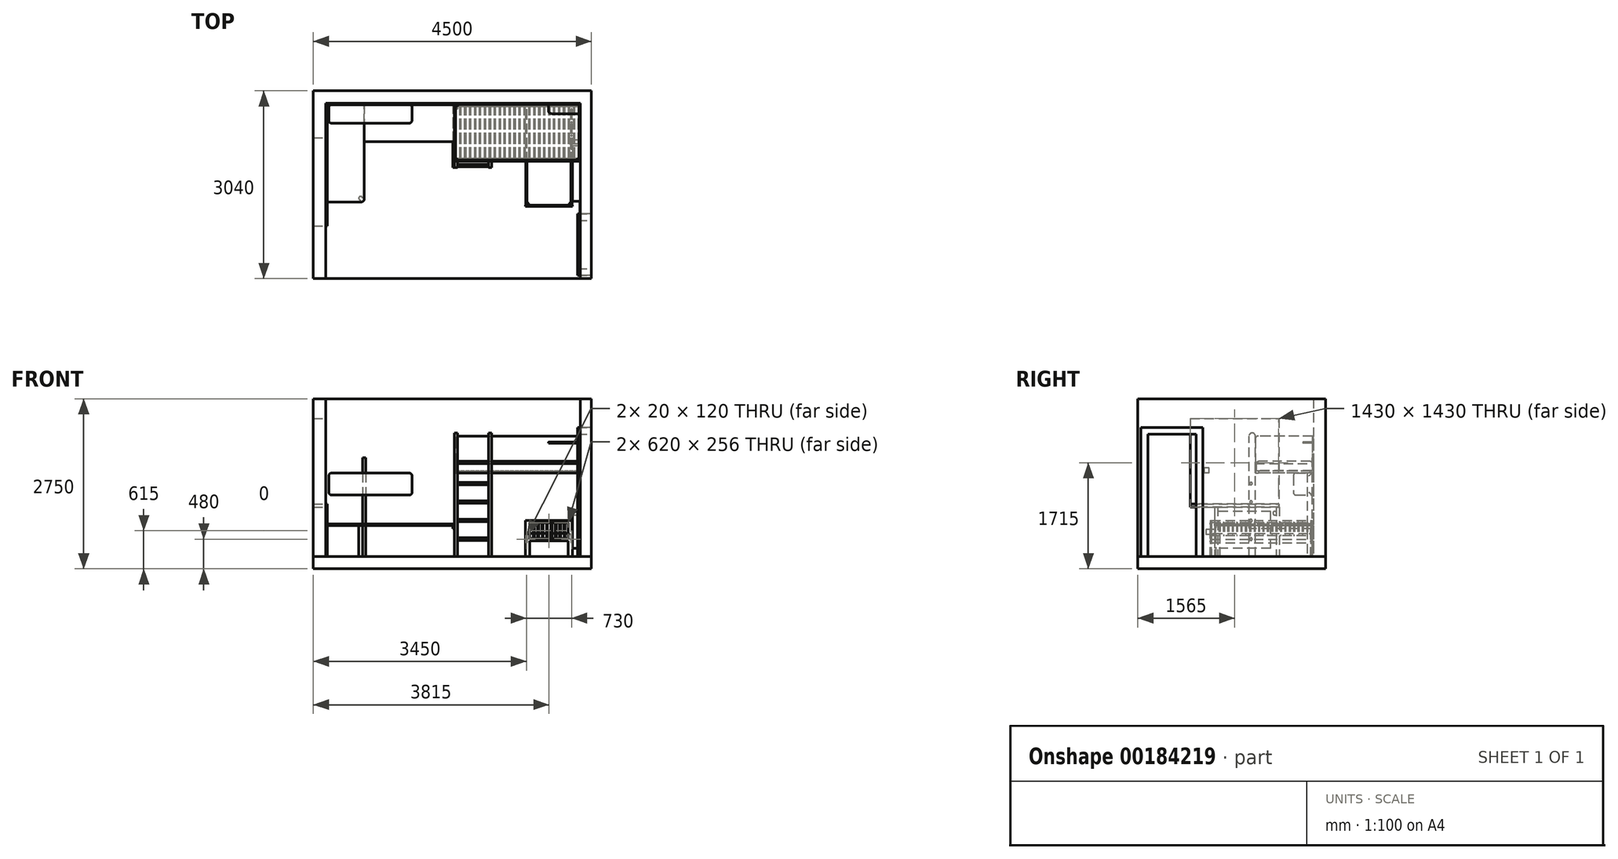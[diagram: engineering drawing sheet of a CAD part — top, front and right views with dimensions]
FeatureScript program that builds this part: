
annotation { "Feature Type Name" : "Feature", "Feature Type Description" : "" }
export const myFeature = defineFeature(function(context is Context, id is Id, definition is map)
    precondition{}
    {
        {
            var Q0;
            Q0=qCreatedBy(makeId("Top.planeOp"),FACE);
            var sketch = newSketch(context, id + "F0", { "sketchPlane" : qUnion([Q0])});
            skLineSegment(sketch, "E0.bottom", {"start": v(-3001.42, -1963.02) * mm, "end": v(-2801.42, -1963.02) * mm});
            skLineSegment(sketch, "E0.left", {"start": v(-3001.42, -1963.02) * mm, "end": v(-3001.42, 1076.98) * mm});
            skLineSegment(sketch, "E0.right", {"start": v(-2801.42, -1963.02) * mm, "end": v(-2801.42, 876.98) * mm});
            skLineSegment(sketch, "E1.bottom", {"start": v(-3001.42, 1076.98) * mm, "end": v(1498.58, 1076.98) * mm});
            skLineSegment(sketch, "E1.top", {"start": v(-2801.42, 876.98) * mm, "end": v(1298.58, 876.98) * mm});
            skLineSegment(sketch, "E2.top", {"start": v(1498.58, -1963.02) * mm, "end": v(1298.58, -1963.02) * mm});
            skLineSegment(sketch, "E2.left", {"start": v(1498.58, 1076.98) * mm, "end": v(1498.58, -1963.02) * mm});
            skLineSegment(sketch, "E2.right", {"start": v(1298.58, 876.98) * mm, "end": v(1298.58, -1963.02) * mm});
            skSolve(sketch);
        }
        {
            var Q0;
            Q0=makeQuery(id+"F0.imprint","IMPRINT",FACE,{"disambiguationData":[TD([[makeQuery(id+"F0.imprint","IMPRINT",EDGE,{"derivedFrom":sQuery(id+"F0.wireOp",EDGE,"E0.bottom")}),1.0]])]});
            extrude(context, id + "F1", {"entities" : qUnion([Q0]), "depth" : 2550 * mm});
        }
        {
            var Q0;
            Q0=makeQuery(id+"F1.opExtrude","SWEPT_FACE",FACE,{"disambiguationData":[OSD([sQuery(id+"F0.wireOp",EDGE,"E2.left")])]});
            var sketch = newSketch(context, id + "F2", { "sketchPlane" : qUnion([Q0])});
            skLineSegment(sketch, "E3.bottom", {"start": v(-1913.02, 0) * mm, "end": v(-913.02, 0) * mm});
            skLineSegment(sketch, "E3.top", {"start": v(-1913.02, 2090) * mm, "end": v(-913.02, 2090) * mm});
            skLineSegment(sketch, "E3.left", {"start": v(-1913.02, 0) * mm, "end": v(-1913.02, 2090) * mm});
            skLineSegment(sketch, "E3.right", {"start": v(-913.02, 0) * mm, "end": v(-913.02, 2090) * mm});
            skSolve(sketch);
        }
        {
            var Q0;
            Q0=makeQuery(id+"F2.imprint","IMPRINT",FACE,{"disambiguationData":[TD([[makeQuery(id+"F2.imprint","IMPRINT",EDGE,{"derivedFrom":sQuery(id+"F2.wireOp",EDGE,"E3.bottom")}),-1.0]])]});
            var Q1;
            Q1=makeQuery(id+"F1.opExtrude","SWEPT_FACE",FACE,{"disambiguationData":[OSD([sQuery(id+"F0.wireOp",EDGE,"E2.right")])]});
            extrude(context, id + "F3", {"entities" : qUnion([Q0, Q1]), "operationType" : NewBodyOperationType.REMOVE, "depth" : 25 * mm, "hasSecondDirection" : true, "secondDirectionBound" : SecondDirectionBoundingType.UP_TO_NEXT, "secondDirectionOppositeDirection" : true, "secondDirectionDepth" : 25 * mm});
        }
        {
            var Q0;
            {var subQ0=sQuery(id+"F0.wireOp",EDGE,"E0.right");var subQ1=sQuery(id+"F0.wireOp",EDGE,"E0.left");var subQ2=sQuery(id+"F0.wireOp",EDGE,"E1.bottom");var subQ3=sQuery(id+"F0.wireOp",EDGE,"E0.bottom");var subQ4=sQuery(id+"F0.wireOp",EDGE,"E1.top");var subQ5=sQuery(id+"F0.wireOp",EDGE,"E2.right");var subQ6=sQuery(id+"F0.wireOp",EDGE,"E2.left");Q0=makeQuery(id+"F3.boolean.opBoolean","SPLIT",FACE,{"disambiguationData":[TD([makeQuery(id+"F1.opExtrude","SWEPT_FACE",FACE,{"disambiguationData":[OSD([subQ3])]})])],"derivedFrom":makeQuery(id+"F1.opExtrude","CAP_FACE",FACE,{"disambiguationData":[OSD([subQ3,subQ1,subQ0,subQ2,subQ4,sQuery(id+"F0.wireOp",EDGE,"E2.top"),subQ6,subQ5])],"isStart":true})});}
            var sketch = newSketch(context, id + "F4", { "sketchPlane" : qUnion([Q0])});
            skLineSegment(sketch, "E4.bottom", {"start": v(-3001.42, 1963.02) * mm, "end": v(1498.58, 1963.02) * mm});
            skLineSegment(sketch, "E4.top", {"start": v(-3001.42, -1076.98) * mm, "end": v(1498.58, -1076.98) * mm});
            skLineSegment(sketch, "E4.left", {"start": v(-3001.42, 1963.02) * mm, "end": v(-3001.42, -1076.98) * mm});
            skLineSegment(sketch, "E4.right", {"start": v(1498.58, 1963.02) * mm, "end": v(1498.58, -1076.98) * mm});
            skSolve(sketch);
        }
        {
            var Q0;
            Q0 = qSketchRegion(id + "F4", true);
            extrude(context, id + "F5", {"entities" : qUnion([Q0]), "depth" : 200 * mm});
        }
        {
            var Q0;
            Q0=makeQuery(id+"F1.opExtrude","SWEPT_FACE",FACE,{"disambiguationData":[OSD([sQuery(id+"F0.wireOp",EDGE,"E0.right")])]});
            var sketch = newSketch(context, id + "F6", { "sketchPlane" : qUnion([Q0])});
            skLineSegment(sketch, "E5.bottom", {"start": v(6034.41, -2246.1) * mm, "end": v(2051.9, -2246.1) * mm});
            skLineSegment(sketch, "E5.top", {"start": v(6034.41, 0) * mm, "end": v(2051.9, 0) * mm});
            skLineSegment(sketch, "E5.left", {"start": v(6034.41, -2246.1) * mm, "end": v(6034.41, 0) * mm});
            skLineSegment(sketch, "E5.right", {"start": v(2051.9, -2246.1) * mm, "end": v(2051.9, 0) * mm});
            skLineSegment(sketch, "E6.bottom", {"start": v(-1113.02, 2230) * mm, "end": v(316.98, 2230) * mm});
            skLineSegment(sketch, "E6.top", {"start": v(-1113.02, 800) * mm, "end": v(316.98, 800) * mm});
            skLineSegment(sketch, "E6.left", {"start": v(-1113.02, 2230) * mm, "end": v(-1113.02, 800) * mm});
            skLineSegment(sketch, "E6.right", {"start": v(316.98, 2230) * mm, "end": v(316.98, 800) * mm});
            skSolve(sketch);
        }
        {
            var Q0;
            Q0 = qSketchRegion(id + "F6", true);
            var Q1;
            Q1=makeQuery(id+"F5.boolean.opBoolean","MERGE",FACE,{"derivedFrom":[makeQuery(id+"F1.opExtrude","SWEPT_FACE",FACE,{"disambiguationData":[OSD([sQuery(id+"F0.wireOp",EDGE,"E0.left")])]}),makeQuery(id+"F5.opExtrude","SWEPT_FACE",FACE,{"disambiguationData":[OSD([sQuery(id+"F4.wireOp",EDGE,"E4.left")])]})]});
            extrude(context, id + "F7", {"entities" : qUnion([Q0]), "operationType" : NewBodyOperationType.REMOVE, "endBound" : BoundingType.UP_TO_SURFACE, "oppositeDirection" : true, "endBoundEntityFace" : qUnion([Q1]), "depth" : 25 * mm});
        }
        {
            var Q0;
            Q0=makeQuery(id+"F5.boolean.opBoolean","MERGE",FACE,{"derivedFrom":[makeQuery(id+"F1.opExtrude","SWEPT_FACE",FACE,{"disambiguationData":[OSD([sQuery(id+"F0.wireOp",EDGE,"E2.left")])]}),makeQuery(id+"F5.opExtrude","SWEPT_FACE",FACE,{"disambiguationData":[OSD([sQuery(id+"F4.wireOp",EDGE,"E4.right")])]})]});
            var sketch = newSketch(context, id + "F8", { "sketchPlane" : qUnion([Q0])});
            skLineSegment(sketch, "E7.bottom", {"start": v(-1803.02, 1980) * mm, "end": v(-1023.02, 1980) * mm});
            skLineSegment(sketch, "E7.left", {"start": v(-1803.02, 1980) * mm, "end": v(-1803.02, 0) * mm});
            skLineSegment(sketch, "E7.right", {"start": v(-1023.02, 1980) * mm, "end": v(-1023.02, 0) * mm});
            skLineSegment(sketch, "E8.bottom", {"start": v(-1913.02, 2090) * mm, "end": v(-913.02, 2090) * mm});
            skLineSegment(sketch, "E8.top", {"start": v(-1913.02, 0) * mm, "end": v(-1803.02, 0) * mm});
            skLineSegment(sketch, "E8.left", {"start": v(-1913.02, 2090) * mm, "end": v(-1913.02, 0) * mm});
            skLineSegment(sketch, "E8.right", {"start": v(-913.02, 2090) * mm, "end": v(-913.02, 0) * mm});
            skLineSegment(sketch, "E9.trimOffspring", {"start": v(-1023.02, 0) * mm, "end": v(-913.02, 0) * mm});
            skSolve(sketch);
        }
        {
            var Q0;
            Q0 = qSketchRegion(id + "F8", true);
            extrude(context, id + "F9", {"entities" : qUnion([Q0]), "oppositeDirection" : true, "depth" : 220 * mm});
        }
        {
            var Q0;
            Q0=makeQuery(id+"F7.boolean.opBoolean","COPY",FACE,{"derivedFrom":makeQuery(id+"F7.opExtrude","SWEPT_FACE",FACE,{"disambiguationData":[OSD([sQuery(id+"F6.wireOp",EDGE,"E6.top")])]})});
            var sketch = newSketch(context, id + "F10", { "sketchPlane" : qUnion([Q0])});
            skLineSegment(sketch, "E10.bottom", {"start": v(-3001.42, 316.98) * mm, "end": v(-2776.42, 316.98) * mm});
            skLineSegment(sketch, "E10.top", {"start": v(-3001.42, -1113.02) * mm, "end": v(-2776.42, -1113.02) * mm});
            skLineSegment(sketch, "E10.left", {"start": v(-3001.42, 316.98) * mm, "end": v(-3001.42, -1113.02) * mm});
            skLineSegment(sketch, "E10.right", {"start": v(-2776.42, 316.98) * mm, "end": v(-2776.42, -1113.02) * mm});
            skSolve(sketch);
        }
        {
            var Q0;
            Q0 = qSketchRegion(id + "F10", true);
            extrude(context, id + "F11", {"entities" : qUnion([Q0]), "depth" : 50 * mm});
        }
        {
            var Q0;
            Q0=makeQuery(id+"F3.boolean.opBoolean","COPY",FACE,{"derivedFrom":makeQuery(id+"F3.opExtrude","CAP_FACE",FACE,{"disambiguationData":[OSD([sQuery(id+"F0.wireOp",EDGE,"E2.right")])],"isStart":false})});
            var sketch = newSketch(context, id + "F12", { "sketchPlane" : qUnion([Q0])});
            skLineSegment(sketch, "E11.bottom", {"start": v(-186.98, 130) * mm, "end": v(713.02, 130) * mm});
            skLineSegment(sketch, "E11.top", {"start": v(-186.98, 730) * mm, "end": v(713.02, 730) * mm});
            skLineSegment(sketch, "E11.left", {"start": v(-186.98, 130) * mm, "end": v(-186.98, 730) * mm});
            skLineSegment(sketch, "E11.right", {"start": v(713.02, 130) * mm, "end": v(713.02, 730) * mm});
            skSolve(sketch);
        }
        {
            var Q0;
            Q0 = qSketchRegion(id + "F12", true);
            extrude(context, id + "F13", {"entities" : qUnion([Q0]), "depth" : 130 * mm});
        }
        {
            var Q0;
            Q0=makeQuery(id+"F3.boolean.opBoolean","COPY",FACE,{"derivedFrom":makeQuery(id+"F3.opExtrude","CAP_FACE",FACE,{"disambiguationData":[OSD([sQuery(id+"F0.wireOp",EDGE,"E2.right")])],"isStart":false})});
            var sketch = newSketch(context, id + "F14", { "sketchPlane" : qUnion([Q0])});
            skCircle(sketch, "E12", {"center": v(-251.98, 700) * mm, "radius": 30 * mm});
            skSolve(sketch);
        }
        {
            var Q0;
            Q0 = qSketchRegion(id + "F14", true);
            extrude(context, id + "F15", {"entities" : qUnion([Q0]), "depth" : 180 * mm});
        }
        {
            var Q0;
            Q0=makeQuery(id+"F3.boolean.opBoolean","COPY",FACE,{"derivedFrom":makeQuery(id+"F3.opExtrude","CAP_FACE",FACE,{"disambiguationData":[OSD([sQuery(id+"F0.wireOp",EDGE,"E2.right")])],"isStart":false})});
            var sketch = newSketch(context, id + "F16", { "sketchPlane" : qUnion([Q0])});
            skLineSegment(sketch, "E13.bottom", {"start": v(713.02, 435) * mm, "end": v(863.02, 435) * mm});
            skLineSegment(sketch, "E13.top", {"start": v(713.02, 355) * mm, "end": v(863.02, 355) * mm});
            skLineSegment(sketch, "E13.left", {"start": v(713.02, 435) * mm, "end": v(713.02, 355) * mm});
            skLineSegment(sketch, "E13.right", {"start": v(863.02, 435) * mm, "end": v(863.02, 355) * mm});
            skSolve(sketch);
        }
        {
            var Q0;
            Q0 = qSketchRegion(id + "F16", true);
            extrude(context, id + "F17", {"entities" : qUnion([Q0]), "depth" : 10 * mm});
        }
        {
            var Q0;
            Q0=makeQuery(id+"F3.boolean.opBoolean","COPY",FACE,{"derivedFrom":makeQuery(id+"F3.opExtrude","CAP_FACE",FACE,{"disambiguationData":[OSD([sQuery(id+"F0.wireOp",EDGE,"E2.right")])],"isStart":false})});
            var sketch = newSketch(context, id + "F18", { "sketchPlane" : qUnion([Q0])});
            skLineSegment(sketch, "E14.bottom", {"start": v(808.02, 1350) * mm, "end": v(888.02, 1350) * mm});
            skLineSegment(sketch, "E14.top", {"start": v(808.02, 1430) * mm, "end": v(888.02, 1430) * mm});
            skLineSegment(sketch, "E14.left", {"start": v(808.02, 1350) * mm, "end": v(808.02, 1430) * mm});
            skLineSegment(sketch, "E14.right", {"start": v(888.02, 1350) * mm, "end": v(888.02, 1430) * mm});
            skSolve(sketch);
        }
        {
            var Q0;
            Q0 = qSketchRegion(id + "F18", true);
            extrude(context, id + "F19", {"entities" : qUnion([Q0]), "depth" : 10 * mm});
        }
        {
            var Q0;
            {var subQ0=sQuery(id+"F0.wireOp",EDGE,"E1.top");Q0=makeQuery(id+"F3.boolean.opBoolean","MERGE",FACE,{"derivedFrom":[makeQuery(id+"F1.opExtrude","SWEPT_FACE",FACE,{"disambiguationData":[OSD([subQ0])]})],"fromTools":[makeQuery(id+"F3.opExtrude","SWEPT_FACE",FACE,{"disambiguationData":[OSD([subQ0,sQuery(id+"F0.wireOp",EDGE,"E2.right")])]})]});}
            var sketch = newSketch(context, id + "F20", { "sketchPlane" : qUnion([Q0])});
            skLineSegment(sketch, "E15.bottom", {"start": v(433.58, 580) * mm, "end": v(1193.58, 580) * mm});
            skLineSegment(sketch, "E15.top", {"start": v(433.58, 0) * mm, "end": v(503.58, 0) * mm});
            skLineSegment(sketch, "E15.left", {"start": v(433.58, 580) * mm, "end": v(433.58, 0) * mm});
            skLineSegment(sketch, "E15.right", {"start": v(1193.58, 580) * mm, "end": v(1193.58, 0) * mm});
            skLineSegment(sketch, "E16.top", {"start": v(503.58, 250) * mm, "end": v(1123.58, 250) * mm});
            skLineSegment(sketch, "E16.left", {"start": v(503.58, 0) * mm, "end": v(503.58, 250) * mm});
            skLineSegment(sketch, "E16.right", {"start": v(1123.58, 0) * mm, "end": v(1123.58, 250) * mm});
            skLineSegment(sketch, "E17.trimOffspring", {"start": v(1123.58, 0) * mm, "end": v(1193.58, 0) * mm});
            skLineSegment(sketch, "E18.bottom", {"start": v(503.58, 287) * mm, "end": v(1123.58, 287) * mm});
            skLineSegment(sketch, "E18.top", {"start": v(503.58, 543) * mm, "end": v(1123.58, 543) * mm});
            skLineSegment(sketch, "E18.left", {"start": v(503.58, 287) * mm, "end": v(503.58, 543) * mm});
            skLineSegment(sketch, "E18.right", {"start": v(1123.58, 287) * mm, "end": v(1123.58, 543) * mm});
            skSolve(sketch);
        }
        {
            var Q0;
            Q0=makeQuery(id+"F20.imprint","IMPRINT",FACE,{"disambiguationData":[TD([[makeQuery(id+"F20.imprint","IMPRINT",EDGE,{"derivedFrom":sQuery(id+"F20.wireOp",EDGE,"E15.bottom")}),-1.0]])]});
            extrude(context, id + "F21", {"entities" : qUnion([Q0]), "depth" : 40 * mm, "hasSecondDirection" : true, "secondDirectionOppositeDirection" : false, "secondDirectionDepth" : 20 * mm});
        }
        {
            var Q0;
            Q0=makeQuery(id+"F21.opExtrude","SWEPT_FACE",FACE,{"disambiguationData":[OSD([sQuery(id+"F20.wireOp",EDGE,"E18.bottom")])]});
            var sketch = newSketch(context, id + "F22", { "sketchPlane" : qUnion([Q0])});
            skCircle(sketch, "E19", {"center": v(566.58, 846.98) * mm, "radius": 8 * mm});
            skCircle(sketch, "E20.1.0.0", {"center": v(637.58, 846.98) * mm, "radius": 8 * mm});
            skCircle(sketch, "E20.2.0.0", {"center": v(708.58, 846.98) * mm, "radius": 8 * mm});
            skCircle(sketch, "E20.3.0.0", {"center": v(779.58, 846.98) * mm, "radius": 8 * mm});
            skCircle(sketch, "E20.4.0.0", {"center": v(850.58, 846.98) * mm, "radius": 8 * mm});
            skCircle(sketch, "E20.5.0.0", {"center": v(921.58, 846.98) * mm, "radius": 8 * mm});
            skCircle(sketch, "E20.6.0.0", {"center": v(992.58, 846.98) * mm, "radius": 8 * mm});
            skCircle(sketch, "E20.7.0.0", {"center": v(1063.58, 846.98) * mm, "radius": 8 * mm});
            skLineSegment(sketch, "E20.direction1", {"start": v(566.58, 846.98) * mm, "end": v(637.58, 846.98) * mm, "construction": true});
            skSolve(sketch);
        }
        {
            var Q0;
            Q0 = qSketchRegion(id + "F22", true);
            var Q1;
            Q1=makeQuery(id+"F21.opExtrude","SWEPT_FACE",FACE,{"disambiguationData":[OSD([sQuery(id+"F20.wireOp",EDGE,"E18.top")])]});
            extrude(context, id + "F23", {"entities" : qUnion([Q0]), "operationType" : NewBodyOperationType.ADD, "endBound" : BoundingType.UP_TO_SURFACE, "endBoundEntityFace" : qUnion([Q1]), "depth" : 25 * mm});
        }
        {
            var Q0;
            Q0 = qSketchRegion(id + "F20", true);
            extrude(context, id + "F24", {"entities" : qUnion([Q0]), "depth" : 1670 * mm, "hasSecondDirection" : true, "secondDirectionOppositeDirection" : false, "secondDirectionDepth" : 1650 * mm});
        }
        {
            var Q0;
            Q0=makeQuery(id+"F24.opExtrude","SWEPT_FACE",FACE,{"disambiguationData":[OSD([sQuery(id+"F20.wireOp",EDGE,"E18.bottom")])]});
            var sketch = newSketch(context, id + "F25", { "sketchPlane" : qUnion([Q0])});
            skCircle(sketch, "E21", {"center": v(568.58, -783.02) * mm, "radius": 8 * mm});
            skCircle(sketch, "E22.1.0.0", {"center": v(639.58, -783.02) * mm, "radius": 8 * mm});
            skCircle(sketch, "E22.2.0.0", {"center": v(710.58, -783.02) * mm, "radius": 8 * mm});
            skCircle(sketch, "E22.3.0.0", {"center": v(781.58, -783.02) * mm, "radius": 8 * mm});
            skCircle(sketch, "E22.4.0.0", {"center": v(852.58, -783.02) * mm, "radius": 8 * mm});
            skCircle(sketch, "E22.5.0.0", {"center": v(923.58, -783.02) * mm, "radius": 8 * mm});
            skCircle(sketch, "E22.6.0.0", {"center": v(994.58, -783.02) * mm, "radius": 8 * mm});
            skCircle(sketch, "E22.7.0.0", {"center": v(1065.58, -783.02) * mm, "radius": 8 * mm});
            skLineSegment(sketch, "E22.direction1", {"start": v(568.58, -783.02) * mm, "end": v(639.58, -783.02) * mm, "construction": true});
            skSolve(sketch);
        }
        {
            var Q0;
            Q0 = qSketchRegion(id + "F25", true);
            var Q1;
            Q1=makeQuery(id+"F24.opExtrude","SWEPT_FACE",FACE,{"disambiguationData":[OSD([sQuery(id+"F20.wireOp",EDGE,"E18.top")])]});
            extrude(context, id + "F26", {"entities" : qUnion([Q0]), "operationType" : NewBodyOperationType.ADD, "endBound" : BoundingType.UP_TO_SURFACE, "endBoundEntityFace" : qUnion([Q1]), "depth" : 25 * mm});
        }
        {
            var Q0;
            Q0=makeQuery(id+"F21.opExtrude","CAP_FACE",FACE,{"disambiguationData":[OSD([sQuery(id+"F20.wireOp",EDGE,"E15.bottom"),sQuery(id+"F20.wireOp",EDGE,"E15.top"),sQuery(id+"F20.wireOp",EDGE,"E15.left"),sQuery(id+"F20.wireOp",EDGE,"E15.right"),sQuery(id+"F20.wireOp",EDGE,"E16.top"),sQuery(id+"F20.wireOp",EDGE,"E16.left"),sQuery(id+"F20.wireOp",EDGE,"E16.right"),sQuery(id+"F20.wireOp",EDGE,"E17.trimOffspring"),sQuery(id+"F20.wireOp",EDGE,"E18.bottom"),sQuery(id+"F20.wireOp",EDGE,"E18.top"),sQuery(id+"F20.wireOp",EDGE,"E18.left"),sQuery(id+"F20.wireOp",EDGE,"E18.right")])],"isStart":false});
            var sketch = newSketch(context, id + "F27", { "sketchPlane" : qUnion([Q0])});
            skLineSegment(sketch, "E23.bottom", {"start": v(438.58, 340) * mm, "end": v(458.58, 340) * mm});
            skLineSegment(sketch, "E23.top", {"start": v(438.58, 220) * mm, "end": v(458.58, 220) * mm});
            skLineSegment(sketch, "E23.left", {"start": v(438.58, 340) * mm, "end": v(438.58, 220) * mm});
            skLineSegment(sketch, "E23.right", {"start": v(458.58, 340) * mm, "end": v(458.58, 220) * mm});
            skLineSegment(sketch, "E24", {"start": v(813.58, 580) * mm, "end": v(813.58, 240.29) * mm, "construction": true});
            skLineSegment(sketch, "E25.MirrorCS", {"start": v(1188.58, 340) * mm, "end": v(1168.58, 340) * mm});
            skLineSegment(sketch, "E26.MirrorCS", {"start": v(1188.58, 220) * mm, "end": v(1168.58, 220) * mm});
            skLineSegment(sketch, "E27.MirrorCS", {"start": v(1168.58, 340) * mm, "end": v(1168.58, 220) * mm});
            skLineSegment(sketch, "E28.MirrorCS", {"start": v(1188.58, 340) * mm, "end": v(1188.58, 220) * mm});
            skLineSegment(sketch, "E29.bottom", {"start": v(1168.58, 580) * mm, "end": v(1188.58, 580) * mm});
            skLineSegment(sketch, "E29.top", {"start": v(1168.58, 550) * mm, "end": v(1188.58, 550) * mm});
            skLineSegment(sketch, "E29.left", {"start": v(1168.58, 580) * mm, "end": v(1168.58, 550) * mm});
            skLineSegment(sketch, "E29.right", {"start": v(1188.58, 580) * mm, "end": v(1188.58, 550) * mm});
            skSolve(sketch);
        }
        {
            var Q0;
            Q0 = qSketchRegion(id + "F27", true);
            extrude(context, id + "F28", {"entities" : qUnion([Q0]), "operationType" : NewBodyOperationType.ADD, "endBound" : BoundingType.UP_TO_NEXT, "depth" : 25 * mm});
        }
        {
            var Q0;
            Q0=makeQuery(id+"F28.opExtrude","SWEPT_FACE",FACE,{"disambiguationData":[OSD([sQuery(id+"F27.wireOp",EDGE,"E25.MirrorCS")])]});
            var sketch = newSketch(context, id + "F29", { "sketchPlane" : qUnion([Q0])});
            skCircle(sketch, "E30", {"center": v(1178.58, 776.98) * mm, "radius": 8 * mm});
            skCircle(sketch, "E31.0.1.0", {"center": v(1178.58, 705.98) * mm, "radius": 8 * mm});
            skCircle(sketch, "E31.0.2.0", {"center": v(1178.58, 634.98) * mm, "radius": 8 * mm});
            skCircle(sketch, "E31.0.3.0", {"center": v(1178.58, 563.98) * mm, "radius": 8 * mm});
            skCircle(sketch, "E31.0.4.0", {"center": v(1178.58, 492.98) * mm, "radius": 8 * mm});
            skCircle(sketch, "E31.0.5.0", {"center": v(1178.58, 421.98) * mm, "radius": 8 * mm});
            skCircle(sketch, "E31.0.6.0", {"center": v(1178.58, 350.98) * mm, "radius": 8 * mm});
            skCircle(sketch, "E31.0.7.0", {"center": v(1178.58, 279.98) * mm, "radius": 8 * mm});
            skCircle(sketch, "E31.0.8.0", {"center": v(1178.58, 208.98) * mm, "radius": 8 * mm});
            skCircle(sketch, "E31.0.9.0", {"center": v(1178.58, 137.98) * mm, "radius": 8 * mm});
            skCircle(sketch, "E31.0.10.0", {"center": v(1178.58, 66.98) * mm, "radius": 8 * mm});
            skCircle(sketch, "E31.0.11.0", {"center": v(1178.58, -4.02) * mm, "radius": 8 * mm});
            skCircle(sketch, "E31.0.12.0", {"center": v(1178.58, -75.02) * mm, "radius": 8 * mm});
            skCircle(sketch, "E31.0.13.0", {"center": v(1178.58, -146.02) * mm, "radius": 8 * mm});
            skCircle(sketch, "E31.0.14.0", {"center": v(1178.58, -217.02) * mm, "radius": 8 * mm});
            skCircle(sketch, "E31.0.15.0", {"center": v(1178.58, -288.02) * mm, "radius": 8 * mm});
            skCircle(sketch, "E31.0.16.0", {"center": v(1178.58, -359.02) * mm, "radius": 8 * mm});
            skCircle(sketch, "E31.0.17.0", {"center": v(1178.58, -430.02) * mm, "radius": 8 * mm});
            skCircle(sketch, "E31.0.18.0", {"center": v(1178.58, -501.02) * mm, "radius": 8 * mm});
            skCircle(sketch, "E31.0.19.0", {"center": v(1178.58, -572.02) * mm, "radius": 8 * mm});
            skCircle(sketch, "E31.0.20.0", {"center": v(1178.58, -643.02) * mm, "radius": 8 * mm});
            skCircle(sketch, "E31.0.21.0", {"center": v(1178.58, -714.02) * mm, "radius": 8 * mm});
            skLineSegment(sketch, "E31.direction1", {"start": v(1178.58, 776.98) * mm, "end": v(1203.58, 776.98) * mm, "construction": true});
            skLineSegment(sketch, "E31.direction2", {"start": v(1178.58, 776.98) * mm, "end": v(1178.58, 705.98) * mm, "construction": true});
            skSolve(sketch);
        }
        {
            var Q0;
            Q0 = qSketchRegion(id + "F29", true);
            extrude(context, id + "F30", {"entities" : qUnion([Q0]), "operationType" : NewBodyOperationType.ADD, "endBound" : BoundingType.UP_TO_NEXT, "depth" : 25 * mm});
        }
        {
            var Q0;
            Q0=makeQuery(id+"F21.opExtrude","CAP_FACE",FACE,{"disambiguationData":[OSD([sQuery(id+"F20.wireOp",EDGE,"E15.bottom"),sQuery(id+"F20.wireOp",EDGE,"E15.top"),sQuery(id+"F20.wireOp",EDGE,"E15.left"),sQuery(id+"F20.wireOp",EDGE,"E15.right"),sQuery(id+"F20.wireOp",EDGE,"E16.top"),sQuery(id+"F20.wireOp",EDGE,"E16.left"),sQuery(id+"F20.wireOp",EDGE,"E16.right"),sQuery(id+"F20.wireOp",EDGE,"E17.trimOffspring"),sQuery(id+"F20.wireOp",EDGE,"E18.bottom"),sQuery(id+"F20.wireOp",EDGE,"E18.top"),sQuery(id+"F20.wireOp",EDGE,"E18.left"),sQuery(id+"F20.wireOp",EDGE,"E18.right")])],"isStart":false});
            var sketch = newSketch(context, id + "F31", { "sketchPlane" : qUnion([Q0])});
            skLineSegment(sketch, "E32.bottom", {"start": v(1168.58, 280) * mm, "end": v(458.58, 280) * mm});
            skLineSegment(sketch, "E32.top", {"start": v(1168.58, 370) * mm, "end": v(458.58, 370) * mm});
            skLineSegment(sketch, "E32.left", {"start": v(1168.58, 280) * mm, "end": v(1168.58, 370) * mm});
            skLineSegment(sketch, "E32.right", {"start": v(458.58, 280) * mm, "end": v(458.58, 370) * mm});
            skSolve(sketch);
        }
        {
            var Q0;
            Q0 = qSketchRegion(id + "F31", true);
            var Q1;
            Q1=makeQuery(id+"F24.opExtrude","CAP_FACE",FACE,{"disambiguationData":[OSD([sQuery(id+"F20.wireOp",EDGE,"E15.bottom"),sQuery(id+"F20.wireOp",EDGE,"E15.top"),sQuery(id+"F20.wireOp",EDGE,"E15.left"),sQuery(id+"F20.wireOp",EDGE,"E15.right"),sQuery(id+"F20.wireOp",EDGE,"E16.top"),sQuery(id+"F20.wireOp",EDGE,"E16.left"),sQuery(id+"F20.wireOp",EDGE,"E16.right"),sQuery(id+"F20.wireOp",EDGE,"E17.trimOffspring"),sQuery(id+"F20.wireOp",EDGE,"E18.bottom"),sQuery(id+"F20.wireOp",EDGE,"E18.top"),sQuery(id+"F20.wireOp",EDGE,"E18.left"),sQuery(id+"F20.wireOp",EDGE,"E18.right")])],"isStart":true});
            extrude(context, id + "F32", {"entities" : qUnion([Q0]), "endBound" : BoundingType.UP_TO_SURFACE, "endBoundEntityFace" : qUnion([Q1]), "depth" : 25 * mm});
        }
        {
            var Q0;
            Q0=makeQuery(id+"F3.boolean.opBoolean","COPY",FACE,{"derivedFrom":makeQuery(id+"F3.opExtrude","CAP_FACE",FACE,{"disambiguationData":[OSD([sQuery(id+"F0.wireOp",EDGE,"E2.right")])],"isStart":false})});
            var sketch = newSketch(context, id + "F33", { "sketchPlane" : qUnion([Q0])});
            skLineSegment(sketch, "E33.bottom", {"start": v(-876.98, 1950) * mm, "end": v(-856.98, 1950) * mm});
            skLineSegment(sketch, "E33.top", {"start": v(-876.98, 1350) * mm, "end": v(-856.98, 1350) * mm});
            skLineSegment(sketch, "E33.left", {"start": v(-876.98, 1950) * mm, "end": v(-876.98, 1350) * mm});
            skLineSegment(sketch, "E33.right", {"start": v(-856.98, 1950) * mm, "end": v(-856.98, 1350) * mm});
            skLineSegment(sketch, "E34.bottom", {"start": v(-856.98, 1350) * mm, "end": v(-826.98, 1350) * mm});
            skLineSegment(sketch, "E34.top", {"start": v(-856.98, 1380) * mm, "end": v(-826.98, 1380) * mm});
            skLineSegment(sketch, "E34.left", {"start": v(-856.98, 1350) * mm, "end": v(-856.98, 1380) * mm});
            skLineSegment(sketch, "E34.right", {"start": v(-826.98, 1350) * mm, "end": v(-826.98, 1380) * mm});
            skLineSegment(sketch, "E35.bottom", {"start": v(-856.98, 1380) * mm, "end": v(43.02, 1380) * mm});
            skLineSegment(sketch, "E35.top", {"start": v(-856.98, 1390) * mm, "end": v(43.02, 1390) * mm});
            skLineSegment(sketch, "E35.left", {"start": v(-856.98, 1380) * mm, "end": v(-856.98, 1390) * mm});
            skLineSegment(sketch, "E35.right", {"start": v(43.02, 1380) * mm, "end": v(43.02, 1390) * mm});
            skLineSegment(sketch, "E36.bottom", {"start": v(43.02, 1380) * mm, "end": v(13.02, 1380) * mm});
            skLineSegment(sketch, "E36.top", {"start": v(43.02, 1350) * mm, "end": v(13.02, 1350) * mm});
            skLineSegment(sketch, "E36.left", {"start": v(43.02, 1380) * mm, "end": v(43.02, 1350) * mm});
            skLineSegment(sketch, "E36.right", {"start": v(13.02, 1380) * mm, "end": v(13.02, 1350) * mm});
            skLineSegment(sketch, "E37.bottom", {"start": v(43.02, 1350) * mm, "end": v(63.02, 1350) * mm});
            skLineSegment(sketch, "E37.top", {"start": v(43.02, 1500) * mm, "end": v(63.02, 1500) * mm});
            skLineSegment(sketch, "E37.left", {"start": v(43.02, 1350) * mm, "end": v(43.02, 1500) * mm});
            skLineSegment(sketch, "E37.right", {"start": v(63.02, 1350) * mm, "end": v(63.02, 1500) * mm});
            skSolve(sketch);
        }
        {
            var Q0;
            Q0 = qSketchRegion(id + "F33", true);
            extrude(context, id + "F34", {"entities" : qUnion([Q0]), "depth" : 2020 * mm, "hasSecondDirection" : true, "secondDirectionOppositeDirection" : false, "secondDirectionDepth" : 20 * mm});
        }
        {
            var Q0;
            Q0=makeQuery(id+"F3.boolean.opBoolean","COPY",FACE,{"derivedFrom":makeQuery(id+"F3.opExtrude","CAP_FACE",FACE,{"disambiguationData":[OSD([sQuery(id+"F0.wireOp",EDGE,"E2.right")])],"isStart":false})});
            var sketch = newSketch(context, id + "F35", { "sketchPlane" : qUnion([Q0])});
            skLineSegment(sketch, "E38.bottom", {"start": v(-876.98, 1950) * mm, "end": v(63.02, 1950) * mm});
            skLineSegment(sketch, "E38.top", {"start": v(-876.98, 1350) * mm, "end": v(63.02, 1350) * mm});
            skLineSegment(sketch, "E38.left", {"start": v(-876.98, 1950) * mm, "end": v(-876.98, 1350) * mm});
            skLineSegment(sketch, "E38.right", {"start": v(63.02, 1950) * mm, "end": v(63.02, 1350) * mm});
            skSolve(sketch);
        }
        {
            var Q0;
            Q0 = qSketchRegion(id + "F35", true);
            extrude(context, id + "F36", {"entities" : qUnion([Q0]), "operationType" : NewBodyOperationType.ADD, "depth" : 20 * mm});
        }
        {
            var Q0;
            Q0=makeQuery(id+"F34.opExtrude","SWEPT_FACE",FACE,{"disambiguationData":[OSD([sQuery(id+"F33.wireOp",EDGE,"E35.top")])]});
            var sketch = newSketch(context, id + "F37", { "sketchPlane" : qUnion([Q0])});
            skLineSegment(sketch, "E39.bottom", {"start": v(-636.42, 856.98) * mm, "end": v(-616.42, 856.98) * mm});
            skLineSegment(sketch, "E39.top", {"start": v(-636.42, -43.02) * mm, "end": v(-616.42, -43.02) * mm});
            skLineSegment(sketch, "E39.left", {"start": v(-636.42, 856.98) * mm, "end": v(-636.42, -43.02) * mm});
            skLineSegment(sketch, "E39.right", {"start": v(-616.42, 856.98) * mm, "end": v(-616.42, -43.02) * mm});
            skLineSegment(sketch, "E40.1.0.0", {"start": v(-536.42, 856.98) * mm, "end": v(-536.42, -43.02) * mm});
            skLineSegment(sketch, "E40.1.0.1", {"start": v(-556.42, 856.98) * mm, "end": v(-556.42, -43.02) * mm});
            skLineSegment(sketch, "E40.1.0.2", {"start": v(-556.42, -43.02) * mm, "end": v(-536.42, -43.02) * mm});
            skLineSegment(sketch, "E40.1.0.3", {"start": v(-556.42, 856.98) * mm, "end": v(-536.42, 856.98) * mm});
            skLineSegment(sketch, "E40.2.0.0", {"start": v(-456.42, 856.98) * mm, "end": v(-456.42, -43.02) * mm});
            skLineSegment(sketch, "E40.2.0.1", {"start": v(-476.42, 856.98) * mm, "end": v(-476.42, -43.02) * mm});
            skLineSegment(sketch, "E40.2.0.2", {"start": v(-476.42, -43.02) * mm, "end": v(-456.42, -43.02) * mm});
            skLineSegment(sketch, "E40.2.0.3", {"start": v(-476.42, 856.98) * mm, "end": v(-456.42, 856.98) * mm});
            skLineSegment(sketch, "E40.3.0.0", {"start": v(-376.42, 856.98) * mm, "end": v(-376.42, -43.02) * mm});
            skLineSegment(sketch, "E40.3.0.1", {"start": v(-396.42, 856.98) * mm, "end": v(-396.42, -43.02) * mm});
            skLineSegment(sketch, "E40.3.0.2", {"start": v(-396.42, -43.02) * mm, "end": v(-376.42, -43.02) * mm});
            skLineSegment(sketch, "E40.3.0.3", {"start": v(-396.42, 856.98) * mm, "end": v(-376.42, 856.98) * mm});
            skLineSegment(sketch, "E40.4.0.0", {"start": v(-296.42, 856.98) * mm, "end": v(-296.42, -43.02) * mm});
            skLineSegment(sketch, "E40.4.0.1", {"start": v(-316.42, 856.98) * mm, "end": v(-316.42, -43.02) * mm});
            skLineSegment(sketch, "E40.4.0.2", {"start": v(-316.42, -43.02) * mm, "end": v(-296.42, -43.02) * mm});
            skLineSegment(sketch, "E40.4.0.3", {"start": v(-316.42, 856.98) * mm, "end": v(-296.42, 856.98) * mm});
            skLineSegment(sketch, "E40.5.0.0", {"start": v(-216.42, 856.98) * mm, "end": v(-216.42, -43.02) * mm});
            skLineSegment(sketch, "E40.5.0.1", {"start": v(-236.42, 856.98) * mm, "end": v(-236.42, -43.02) * mm});
            skLineSegment(sketch, "E40.5.0.2", {"start": v(-236.42, -43.02) * mm, "end": v(-216.42, -43.02) * mm});
            skLineSegment(sketch, "E40.5.0.3", {"start": v(-236.42, 856.98) * mm, "end": v(-216.42, 856.98) * mm});
            skLineSegment(sketch, "E40.6.0.0", {"start": v(-136.42, 856.98) * mm, "end": v(-136.42, -43.02) * mm});
            skLineSegment(sketch, "E40.6.0.1", {"start": v(-156.42, 856.98) * mm, "end": v(-156.42, -43.02) * mm});
            skLineSegment(sketch, "E40.6.0.2", {"start": v(-156.42, -43.02) * mm, "end": v(-136.42, -43.02) * mm});
            skLineSegment(sketch, "E40.6.0.3", {"start": v(-156.42, 856.98) * mm, "end": v(-136.42, 856.98) * mm});
            skLineSegment(sketch, "E40.7.0.0", {"start": v(-56.42, 856.98) * mm, "end": v(-56.42, -43.02) * mm});
            skLineSegment(sketch, "E40.7.0.1", {"start": v(-76.42, 856.98) * mm, "end": v(-76.42, -43.02) * mm});
            skLineSegment(sketch, "E40.7.0.2", {"start": v(-76.42, -43.02) * mm, "end": v(-56.42, -43.02) * mm});
            skLineSegment(sketch, "E40.7.0.3", {"start": v(-76.42, 856.98) * mm, "end": v(-56.42, 856.98) * mm});
            skLineSegment(sketch, "E40.8.0.0", {"start": v(23.58, 856.98) * mm, "end": v(23.58, -43.02) * mm});
            skLineSegment(sketch, "E40.8.0.1", {"start": v(3.58, 856.98) * mm, "end": v(3.58, -43.02) * mm});
            skLineSegment(sketch, "E40.8.0.2", {"start": v(3.58, -43.02) * mm, "end": v(23.58, -43.02) * mm});
            skLineSegment(sketch, "E40.8.0.3", {"start": v(3.58, 856.98) * mm, "end": v(23.58, 856.98) * mm});
            skLineSegment(sketch, "E40.9.0.0", {"start": v(103.58, 856.98) * mm, "end": v(103.58, -43.02) * mm});
            skLineSegment(sketch, "E40.9.0.1", {"start": v(83.58, 856.98) * mm, "end": v(83.58, -43.02) * mm});
            skLineSegment(sketch, "E40.9.0.2", {"start": v(83.58, -43.02) * mm, "end": v(103.58, -43.02) * mm});
            skLineSegment(sketch, "E40.9.0.3", {"start": v(83.58, 856.98) * mm, "end": v(103.58, 856.98) * mm});
            skLineSegment(sketch, "E40.10.0.0", {"start": v(183.58, 856.98) * mm, "end": v(183.58, -43.02) * mm});
            skLineSegment(sketch, "E40.10.0.1", {"start": v(163.58, 856.98) * mm, "end": v(163.58, -43.02) * mm});
            skLineSegment(sketch, "E40.10.0.2", {"start": v(163.58, -43.02) * mm, "end": v(183.58, -43.02) * mm});
            skLineSegment(sketch, "E40.10.0.3", {"start": v(163.58, 856.98) * mm, "end": v(183.58, 856.98) * mm});
            skLineSegment(sketch, "E40.11.0.0", {"start": v(263.58, 856.98) * mm, "end": v(263.58, -43.02) * mm});
            skLineSegment(sketch, "E40.11.0.1", {"start": v(243.58, 856.98) * mm, "end": v(243.58, -43.02) * mm});
            skLineSegment(sketch, "E40.11.0.2", {"start": v(243.58, -43.02) * mm, "end": v(263.58, -43.02) * mm});
            skLineSegment(sketch, "E40.11.0.3", {"start": v(243.58, 856.98) * mm, "end": v(263.58, 856.98) * mm});
            skLineSegment(sketch, "E40.12.0.0", {"start": v(343.58, 856.98) * mm, "end": v(343.58, -43.02) * mm});
            skLineSegment(sketch, "E40.12.0.1", {"start": v(323.58, 856.98) * mm, "end": v(323.58, -43.02) * mm});
            skLineSegment(sketch, "E40.12.0.2", {"start": v(323.58, -43.02) * mm, "end": v(343.58, -43.02) * mm});
            skLineSegment(sketch, "E40.12.0.3", {"start": v(323.58, 856.98) * mm, "end": v(343.58, 856.98) * mm});
            skLineSegment(sketch, "E40.13.0.0", {"start": v(423.58, 856.98) * mm, "end": v(423.58, -43.02) * mm});
            skLineSegment(sketch, "E40.13.0.1", {"start": v(403.58, 856.98) * mm, "end": v(403.58, -43.02) * mm});
            skLineSegment(sketch, "E40.13.0.2", {"start": v(403.58, -43.02) * mm, "end": v(423.58, -43.02) * mm});
            skLineSegment(sketch, "E40.13.0.3", {"start": v(403.58, 856.98) * mm, "end": v(423.58, 856.98) * mm});
            skLineSegment(sketch, "E40.14.0.0", {"start": v(503.58, 856.98) * mm, "end": v(503.58, -43.02) * mm});
            skLineSegment(sketch, "E40.14.0.1", {"start": v(483.58, 856.98) * mm, "end": v(483.58, -43.02) * mm});
            skLineSegment(sketch, "E40.14.0.2", {"start": v(483.58, -43.02) * mm, "end": v(503.58, -43.02) * mm});
            skLineSegment(sketch, "E40.14.0.3", {"start": v(483.58, 856.98) * mm, "end": v(503.58, 856.98) * mm});
            skLineSegment(sketch, "E40.15.0.0", {"start": v(583.58, 856.98) * mm, "end": v(583.58, -43.02) * mm});
            skLineSegment(sketch, "E40.15.0.1", {"start": v(563.58, 856.98) * mm, "end": v(563.58, -43.02) * mm});
            skLineSegment(sketch, "E40.15.0.2", {"start": v(563.58, -43.02) * mm, "end": v(583.58, -43.02) * mm});
            skLineSegment(sketch, "E40.15.0.3", {"start": v(563.58, 856.98) * mm, "end": v(583.58, 856.98) * mm});
            skLineSegment(sketch, "E40.16.0.0", {"start": v(663.58, 856.98) * mm, "end": v(663.58, -43.02) * mm});
            skLineSegment(sketch, "E40.16.0.1", {"start": v(643.58, 856.98) * mm, "end": v(643.58, -43.02) * mm});
            skLineSegment(sketch, "E40.16.0.2", {"start": v(643.58, -43.02) * mm, "end": v(663.58, -43.02) * mm});
            skLineSegment(sketch, "E40.16.0.3", {"start": v(643.58, 856.98) * mm, "end": v(663.58, 856.98) * mm});
            skLineSegment(sketch, "E40.17.0.0", {"start": v(743.58, 856.98) * mm, "end": v(743.58, -43.02) * mm});
            skLineSegment(sketch, "E40.17.0.1", {"start": v(723.58, 856.98) * mm, "end": v(723.58, -43.02) * mm});
            skLineSegment(sketch, "E40.17.0.2", {"start": v(723.58, -43.02) * mm, "end": v(743.58, -43.02) * mm});
            skLineSegment(sketch, "E40.17.0.3", {"start": v(723.58, 856.98) * mm, "end": v(743.58, 856.98) * mm});
            skLineSegment(sketch, "E40.18.0.0", {"start": v(823.58, 856.98) * mm, "end": v(823.58, -43.02) * mm});
            skLineSegment(sketch, "E40.18.0.1", {"start": v(803.58, 856.98) * mm, "end": v(803.58, -43.02) * mm});
            skLineSegment(sketch, "E40.18.0.2", {"start": v(803.58, -43.02) * mm, "end": v(823.58, -43.02) * mm});
            skLineSegment(sketch, "E40.18.0.3", {"start": v(803.58, 856.98) * mm, "end": v(823.58, 856.98) * mm});
            skLineSegment(sketch, "E40.19.0.0", {"start": v(903.58, 856.98) * mm, "end": v(903.58, -43.02) * mm});
            skLineSegment(sketch, "E40.19.0.1", {"start": v(883.58, 856.98) * mm, "end": v(883.58, -43.02) * mm});
            skLineSegment(sketch, "E40.19.0.2", {"start": v(883.58, -43.02) * mm, "end": v(903.58, -43.02) * mm});
            skLineSegment(sketch, "E40.19.0.3", {"start": v(883.58, 856.98) * mm, "end": v(903.58, 856.98) * mm});
            skLineSegment(sketch, "E40.20.0.0", {"start": v(983.58, 856.98) * mm, "end": v(983.58, -43.02) * mm});
            skLineSegment(sketch, "E40.20.0.1", {"start": v(963.58, 856.98) * mm, "end": v(963.58, -43.02) * mm});
            skLineSegment(sketch, "E40.20.0.2", {"start": v(963.58, -43.02) * mm, "end": v(983.58, -43.02) * mm});
            skLineSegment(sketch, "E40.20.0.3", {"start": v(963.58, 856.98) * mm, "end": v(983.58, 856.98) * mm});
            skLineSegment(sketch, "E40.21.0.0", {"start": v(1063.58, 856.98) * mm, "end": v(1063.58, -43.02) * mm});
            skLineSegment(sketch, "E40.21.0.1", {"start": v(1043.58, 856.98) * mm, "end": v(1043.58, -43.02) * mm});
            skLineSegment(sketch, "E40.21.0.2", {"start": v(1043.58, -43.02) * mm, "end": v(1063.58, -43.02) * mm});
            skLineSegment(sketch, "E40.21.0.3", {"start": v(1043.58, 856.98) * mm, "end": v(1063.58, 856.98) * mm});
            skLineSegment(sketch, "E40.22.0.0", {"start": v(1143.58, 856.98) * mm, "end": v(1143.58, -43.02) * mm});
            skLineSegment(sketch, "E40.22.0.1", {"start": v(1123.58, 856.98) * mm, "end": v(1123.58, -43.02) * mm});
            skLineSegment(sketch, "E40.22.0.2", {"start": v(1123.58, -43.02) * mm, "end": v(1143.58, -43.02) * mm});
            skLineSegment(sketch, "E40.22.0.3", {"start": v(1123.58, 856.98) * mm, "end": v(1143.58, 856.98) * mm});
            skLineSegment(sketch, "E40.23.0.0", {"start": v(1223.58, 856.98) * mm, "end": v(1223.58, -43.02) * mm});
            skLineSegment(sketch, "E40.23.0.1", {"start": v(1203.58, 856.98) * mm, "end": v(1203.58, -43.02) * mm});
            skLineSegment(sketch, "E40.23.0.2", {"start": v(1203.58, -43.02) * mm, "end": v(1223.58, -43.02) * mm});
            skLineSegment(sketch, "E40.23.0.3", {"start": v(1203.58, 856.98) * mm, "end": v(1223.58, 856.98) * mm});
            skLineSegment(sketch, "E40.24.0.0", {"start": v(1303.58, 856.98) * mm, "end": v(1303.58, -43.02) * mm});
            skLineSegment(sketch, "E40.24.0.1", {"start": v(1283.58, 856.98) * mm, "end": v(1283.58, -43.02) * mm});
            skLineSegment(sketch, "E40.24.0.2", {"start": v(1283.58, -43.02) * mm, "end": v(1303.58, -43.02) * mm});
            skLineSegment(sketch, "E40.24.0.3", {"start": v(1283.58, 856.98) * mm, "end": v(1303.58, 856.98) * mm});
            skLineSegment(sketch, "E40.direction1", {"start": v(-636.42, -43.02) * mm, "end": v(-556.42, -43.02) * mm, "construction": true});
            skSolve(sketch);
        }
        {
            var Q0;
            Q0 = qSketchRegion(id + "F37", true);
            extrude(context, id + "F38", {"entities" : qUnion([Q0]), "operationType" : NewBodyOperationType.REMOVE, "oppositeDirection" : true, "depth" : 10 * mm});
        }
        {
            var Q0;
            Q0=makeQuery(id+"F3.boolean.opBoolean","COPY",FACE,{"derivedFrom":makeQuery(id+"F3.opExtrude","CAP_FACE",FACE,{"disambiguationData":[OSD([sQuery(id+"F0.wireOp",EDGE,"E2.right")])],"isStart":false})});
            var sketch = newSketch(context, id + "F39", { "sketchPlane" : qUnion([Q0])});
            skLineSegment(sketch, "E41.bottom", {"start": v(63.02, 1500) * mm, "end": v(-876.98, 1500) * mm});
            skLineSegment(sketch, "E41.top", {"start": v(63.02, 1350) * mm, "end": v(-876.98, 1350) * mm});
            skLineSegment(sketch, "E41.left", {"start": v(63.02, 1500) * mm, "end": v(63.02, 1350) * mm});
            skLineSegment(sketch, "E41.right", {"start": v(-876.98, 1500) * mm, "end": v(-876.98, 1350) * mm});
            skSolve(sketch);
        }
        {
            var Q0;
            Q0 = qSketchRegion(id + "F39", true);
            extrude(context, id + "F40", {"entities" : qUnion([Q0]), "depth" : 2040 * mm, "hasSecondDirection" : true, "secondDirectionOppositeDirection" : false, "secondDirectionDepth" : 2020 * mm});
        }
        {
            var Q0;
            Q0=makeQuery(id+"F34.opExtrude","SWEPT_FACE",FACE,{"disambiguationData":[OSD([sQuery(id+"F33.wireOp",EDGE,"E37.top")])]});
            var sketch = newSketch(context, id + "F41", { "sketchPlane" : qUnion([Q0])});
            skLineSegment(sketch, "E42.bottom", {"start": v(-715.78, -63.02) * mm, "end": v(-665.78, -63.02) * mm});
            skLineSegment(sketch, "E42.top", {"start": v(-715.78, -163.02) * mm, "end": v(-665.78, -163.02) * mm});
            skLineSegment(sketch, "E42.left", {"start": v(-715.78, -63.02) * mm, "end": v(-715.78, -163.02) * mm});
            skLineSegment(sketch, "E42.right", {"start": v(-665.78, -63.02) * mm, "end": v(-665.78, -163.02) * mm});
            skLineSegment(sketch, "E43.bottom", {"start": v(-165.78, -63.02) * mm, "end": v(-115.78, -63.02) * mm});
            skLineSegment(sketch, "E43.top", {"start": v(-165.78, -163.02) * mm, "end": v(-115.78, -163.02) * mm});
            skLineSegment(sketch, "E43.left", {"start": v(-165.78, -63.02) * mm, "end": v(-165.78, -163.02) * mm});
            skLineSegment(sketch, "E43.right", {"start": v(-115.78, -63.02) * mm, "end": v(-115.78, -163.02) * mm});
            skSolve(sketch);
        }
        {
            var Q0;
            Q0 = qSketchRegion(id + "F41", true);
            extrude(context, id + "F42", {"entities" : qUnion([Q0]), "endBound" : BoundingType.UP_TO_NEXT, "oppositeDirection" : true, "depth" : 25 * mm, "hasSecondDirection" : true, "secondDirectionOppositeDirection" : false, "secondDirectionDepth" : 500 * mm});
        }
        {
            var Q0;
            Q0=makeQuery(id+"F42.opExtrude","SWEPT_FACE",FACE,{"disambiguationData":[OSD([sQuery(id+"F41.wireOp",EDGE,"E43.left")])]});
            var sketch = newSketch(context, id + "F43", { "sketchPlane" : qUnion([Q0])});
            skCircle(sketch, "E44", {"center": v(132.36, 280) * mm, "radius": 20 * mm});
            skCircle(sketch, "E45.0.1.0", {"center": v(132.36, 580) * mm, "radius": 20 * mm});
            skCircle(sketch, "E45.0.2.0", {"center": v(132.36, 880) * mm, "radius": 20 * mm});
            skCircle(sketch, "E45.0.3.0", {"center": v(132.36, 1180) * mm, "radius": 20 * mm});
            skLineSegment(sketch, "E45.direction1", {"start": v(132.36, 300) * mm, "end": v(157.36, 300) * mm, "construction": true});
            skLineSegment(sketch, "E45.direction2", {"start": v(132.36, 300) * mm, "end": v(132.36, 600) * mm, "construction": true});
            skSolve(sketch);
        }
        {
            var Q0;
            Q0 = qSketchRegion(id + "F43", true);
            extrude(context, id + "F44", {"entities" : qUnion([Q0]), "endBound" : BoundingType.UP_TO_NEXT, "depth" : 25 * mm});
        }
        {
            var Q0;
            Q0=makeQuery(id+"F42.opExtrude","CAP_EDGE",EDGE,{"disambiguationData":[OSD([sQuery(id+"F41.wireOp",EDGE,"E42.top")])],"isStart":true});
            var Q1;
            Q1=makeQuery(id+"F42.opExtrude","CAP_EDGE",EDGE,{"disambiguationData":[OSD([sQuery(id+"F41.wireOp",EDGE,"E43.top")])],"isStart":true});
            var Q2;
            Q2=makeQuery(id+"F42.opExtrude","CAP_EDGE",EDGE,{"disambiguationData":[OSD([sQuery(id+"F41.wireOp",EDGE,"E43.bottom")])],"isStart":true});
            var Q3;
            Q3=makeQuery(id+"F42.opExtrude","CAP_EDGE",EDGE,{"disambiguationData":[OSD([sQuery(id+"F41.wireOp",EDGE,"E42.bottom")])],"isStart":true});
            fillet(context, id + "F45", {"entities" : qUnion([Q0, Q1, Q2, Q3]), "radius" : 50 * mm, "tangentPropagation" : true, "allowEdgeOverflow" : false});
        }
        {
            var Q0;
            Q0=makeQuery(id+"F34.opExtrude","CAP_EDGE",EDGE,{"disambiguationData":[OSD([sQuery(id+"F33.wireOp",EDGE,"E33.bottom")])],"isStart":false});
            fillet(context, id + "F46", {"entities" : qUnion([Q0]), "radius" : 50 * mm, "tangentPropagation" : true, "allowEdgeOverflow" : false});
        }
        {
            var Q0;
            Q0=makeQuery(id+"F36.opExtrude","SWEPT_EDGE",EDGE,{"disambiguationData":[OSD([sQuery(id+"F35.wireOp",EDGE,"E38.bottom"),sQuery(id+"F35.wireOp",EDGE,"E38.right")])]});
            fillet(context, id + "F47", {"entities" : qUnion([Q0]), "radius" : 50 * mm, "tangentPropagation" : true, "allowEdgeOverflow" : false});
        }
        {
            var Q0;
            {var subQ10=sQuery(id+"F35.wireOp",EDGE,"E38.top");var subQ28=sQuery(id+"F35.wireOp",EDGE,"E38.right");var subQ44=makeQuery(id+"F34.opExtrude","SWEPT_FACE",FACE,{"disambiguationData":[OSD([sQuery(id+"F33.wireOp",EDGE,"E34.right")])]});var subQ46=sQuery(id+"F37.wireOp",EDGE,"E40.24.0.0");var subQ47=makeQuery(id+"F38.opExtrude","SWEPT_FACE",FACE,{"disambiguationData":[OSD([subQ46])]});var subQ51=sQuery(id+"F35.wireOp",EDGE,"E38.bottom");var subQ52=makeQuery(id+"F36.opExtrude","CAP_FACE",FACE,{"disambiguationData":[OSD([subQ51,subQ10,sQuery(id+"F35.wireOp",EDGE,"E38.left"),subQ28])],"isStart":false});Q0=makeQuery(id+"FqNzfUu08SkVOEf_20.boolean.opBoolean","SPLIT",FACE,{"disambiguationData":[TD([subQ44])],"derivedFrom":makeQuery(id+"F38.boolean.opBoolean","MERGE",FACE,{"derivedFrom":[makeQuery(id+"F36.boolean.opBoolean","SPLIT",FACE,{"disambiguationData":[TD([makeQuery(id+"F34.opExtrude","SWEPT_FACE",FACE,{"disambiguationData":[OSD([sQuery(id+"F33.wireOp",EDGE,"E33.bottom")])]})])],"derivedFrom":subQ52}),makeQuery(id+"F36.boolean.opBoolean","SPLIT",FACE,{"disambiguationData":[TD([subQ44])],"derivedFrom":subQ52}),subQ47]})});}
            var sketch = newSketch(context, id + "F48", { "sketchPlane" : qUnion([Q0])});
            skLineSegment(sketch, "E46.bottom", {"start": v(-856.98, 1540) * mm, "end": v(43.02, 1540) * mm});
            skLineSegment(sketch, "E46.top", {"start": v(-856.98, 1380) * mm, "end": v(43.02, 1380) * mm});
            skLineSegment(sketch, "E46.left", {"start": v(-856.98, 1540) * mm, "end": v(-856.98, 1380) * mm});
            skLineSegment(sketch, "E46.right", {"start": v(43.02, 1540) * mm, "end": v(43.02, 1380) * mm});
            skSolve(sketch);
        }
        {
            var Q0;
            Q0 = qSketchRegion(id + "F48", true);
            var Q1;
            Q1=makeQuery(id+"F40.opExtrude","CAP_FACE",FACE,{"disambiguationData":[OSD([sQuery(id+"F39.wireOp",EDGE,"E41.bottom"),sQuery(id+"F39.wireOp",EDGE,"E41.top"),sQuery(id+"F39.wireOp",EDGE,"E41.left"),sQuery(id+"F39.wireOp",EDGE,"E41.right")])],"isStart":true});
            extrude(context, id + "F49", {"entities" : qUnion([Q0]), "endBound" : BoundingType.UP_TO_SURFACE, "endBoundEntityFace" : qUnion([Q1]), "depth" : 25 * mm});
        }
        {
            var Q0;
            Q0=makeQuery(id+"F49.opExtrude","SWEPT_FACE",FACE,{"disambiguationData":[OSD([sQuery(id+"F48.wireOp",EDGE,"E46.bottom")])]});
            fillet(context, id + "F50", {"entities" : qUnion([Q0]), "radius" : 30 * mm, "tangentPropagation" : true, "allowEdgeOverflow" : false});
        }
        {
            var Q0;
            Q0=makeQuery(id+"F32.opExtrude","SWEPT_FACE",FACE,{"disambiguationData":[OSD([sQuery(id+"F31.wireOp",EDGE,"E32.top")])]});
            fillet(context, id + "F51", {"entities" : qUnion([Q0]), "radius" : 30 * mm, "tangentPropagation" : true, "allowEdgeOverflow" : false});
        }
        {
            var Q0;
            {var subQ0=sQuery(id+"F35.wireOp",EDGE,"E38.top");var subQ1=sQuery(id+"F35.wireOp",EDGE,"E38.right");var subQ2=sQuery(id+"F35.wireOp",EDGE,"E38.bottom");var subQ3=makeQuery(id+"F36.opExtrude","CAP_FACE",FACE,{"disambiguationData":[OSD([subQ2,subQ0,sQuery(id+"F35.wireOp",EDGE,"E38.left"),subQ1])],"isStart":false});Q0=makeQuery(id+"F38.boolean.opBoolean","MERGE",FACE,{"derivedFrom":[makeQuery(id+"F36.boolean.opBoolean","SPLIT",FACE,{"disambiguationData":[TD([makeQuery(id+"F34.opExtrude","SWEPT_FACE",FACE,{"disambiguationData":[OSD([sQuery(id+"F33.wireOp",EDGE,"E33.bottom")])]})])],"derivedFrom":subQ3}),makeQuery(id+"F36.boolean.opBoolean","SPLIT",FACE,{"disambiguationData":[TD([makeQuery(id+"F34.opExtrude","SWEPT_FACE",FACE,{"disambiguationData":[OSD([sQuery(id+"F33.wireOp",EDGE,"E34.right")])]})])],"derivedFrom":subQ3}),makeQuery(id+"F38.opExtrude","SWEPT_FACE",FACE,{"disambiguationData":[OSD([sQuery(id+"F37.wireOp",EDGE,"E40.24.0.0")])]})]});}
            var sketch = newSketch(context, id + "F52", { "sketchPlane" : qUnion([Q0])});
            skLineSegment(sketch, "E47.bottom", {"start": v(-856.98, 1850) * mm, "end": v(-706.98, 1850) * mm});
            skLineSegment(sketch, "E47.top", {"start": v(-856.98, 1830) * mm, "end": v(-706.98, 1830) * mm});
            skLineSegment(sketch, "E47.left", {"start": v(-856.98, 1850) * mm, "end": v(-856.98, 1830) * mm});
            skLineSegment(sketch, "E47.right", {"start": v(-706.98, 1850) * mm, "end": v(-706.98, 1830) * mm});
            skSolve(sketch);
        }
        {
            var Q0;
            Q0 = qSketchRegion(id + "F52", true);
            extrude(context, id + "F53", {"entities" : qUnion([Q0]), "operationType" : NewBodyOperationType.ADD, "depth" : 500 * mm});
        }
        {
            var Q0;
            Q0=makeQuery(id+"F1.opExtrude","SWEPT_FACE",FACE,{"disambiguationData":[OSD([sQuery(id+"F0.wireOp",EDGE,"E0.right")])]});
            var sketch = newSketch(context, id + "F54", { "sketchPlane" : qUnion([Q0])});
            skLineSegment(sketch, "E48.bottom", {"start": v(-723.02, 800) * mm, "end": v(-673.02, 800) * mm});
            skLineSegment(sketch, "E48.top", {"start": v(-723.02, 0) * mm, "end": v(-673.02, 0) * mm});
            skLineSegment(sketch, "E48.left", {"start": v(-723.02, 800) * mm, "end": v(-723.02, 0) * mm});
            skLineSegment(sketch, "E48.right", {"start": v(-673.02, 800) * mm, "end": v(-673.02, 0) * mm});
            skLineSegment(sketch, "E49.bottom", {"start": v(326.98, 800) * mm, "end": v(276.98, 800) * mm});
            skLineSegment(sketch, "E49.top", {"start": v(326.98, 0) * mm, "end": v(276.98, 0) * mm});
            skLineSegment(sketch, "E49.left", {"start": v(326.98, 800) * mm, "end": v(326.98, 0) * mm});
            skLineSegment(sketch, "E49.right", {"start": v(276.98, 800) * mm, "end": v(276.98, 0) * mm});
            skSolve(sketch);
        }
        {
            var Q0;
            Q0 = qSketchRegion(id + "F54", true);
            extrude(context, id + "F55", {"entities" : qUnion([Q0]), "depth" : 25 * mm});
        }
        {
            var Q0;
            {var subQ0=sQuery(id+"F0.wireOp",EDGE,"E1.top");Q0=makeQuery(id+"F3.boolean.opBoolean","MERGE",FACE,{"derivedFrom":[makeQuery(id+"F1.opExtrude","SWEPT_FACE",FACE,{"disambiguationData":[OSD([subQ0])]})],"fromTools":[makeQuery(id+"F3.opExtrude","SWEPT_FACE",FACE,{"disambiguationData":[OSD([subQ0,sQuery(id+"F0.wireOp",EDGE,"E2.right")])]})]});}
            var sketch = newSketch(context, id + "F56", { "sketchPlane" : qUnion([Q0])});
            skLineSegment(sketch, "E50.bottom", {"start": v(-2201.42, 1600) * mm, "end": v(-2151.42, 1600) * mm});
            skLineSegment(sketch, "E50.top", {"start": v(-2201.42, 0) * mm, "end": v(-2151.42, 0) * mm});
            skLineSegment(sketch, "E50.left", {"start": v(-2201.42, 1600) * mm, "end": v(-2201.42, 0) * mm});
            skLineSegment(sketch, "E50.right", {"start": v(-2151.42, 1600) * mm, "end": v(-2151.42, 0) * mm});
            skSolve(sketch);
        }
        {
            var Q0;
            Q0 = qSketchRegion(id + "F56", true);
            extrude(context, id + "F57", {"entities" : qUnion([Q0]), "depth" : 25 * mm});
        }
        {
            var Q0;
            Q0=makeQuery(id+"F42.opExtrude","SWEPT_FACE",FACE,{"disambiguationData":[OSD([sQuery(id+"F41.wireOp",EDGE,"E42.left")])]});
            var sketch = newSketch(context, id + "F58", { "sketchPlane" : qUnion([Q0])});
            skLineSegment(sketch, "E51.bottom", {"start": v(-876.98, 1350) * mm, "end": v(-776.98, 1350) * mm});
            skLineSegment(sketch, "E51.top", {"start": v(-876.98, 0) * mm, "end": v(-776.98, 0) * mm});
            skLineSegment(sketch, "E51.left", {"start": v(-876.98, 1350) * mm, "end": v(-876.98, 0) * mm});
            skLineSegment(sketch, "E51.right", {"start": v(-776.98, 1350) * mm, "end": v(-776.98, 0) * mm});
            skSolve(sketch);
        }
        {
            var Q0;
            Q0 = qSketchRegion(id + "F58", true);
            extrude(context, id + "F59", {"entities" : qUnion([Q0]), "oppositeDirection" : true, "depth" : 50 * mm});
        }
        {
            var Q0;
            Q0=makeQuery(id+"F59.opExtrude","CAP_FACE",FACE,{"disambiguationData":[OSD([sQuery(id+"F58.wireOp",EDGE,"E51.bottom"),sQuery(id+"F58.wireOp",EDGE,"E51.top"),sQuery(id+"F58.wireOp",EDGE,"E51.left"),sQuery(id+"F58.wireOp",EDGE,"E51.right")])],"isStart":true});
            var sketch = newSketch(context, id + "F60", { "sketchPlane" : qUnion([Q0])});
            skLineSegment(sketch, "E52.bottom", {"start": v(-851.98, 525) * mm, "end": v(-251.98, 525) * mm});
            skLineSegment(sketch, "E52.top", {"start": v(-851.98, 500) * mm, "end": v(-251.98, 500) * mm});
            skLineSegment(sketch, "E52.left", {"start": v(-851.98, 525) * mm, "end": v(-851.98, 500) * mm});
            skLineSegment(sketch, "E52.right", {"start": v(-251.98, 525) * mm, "end": v(-251.98, 500) * mm});
            skSolve(sketch);
        }
        {
            var Q0;
            Q0 = qSketchRegion(id + "F60", true);
            var Q1;
            Q1=makeQuery(id+"F57.opExtrude","SWEPT_FACE",FACE,{"disambiguationData":[OSD([sQuery(id+"F56.wireOp",EDGE,"E50.right")])]});
            extrude(context, id + "F61", {"entities" : qUnion([Q0]), "endBoundEntityFace" : qUnion([Q1]), "depth" : 1460 * mm});
        }
        {
            var Q0;
            Q0=makeQuery(id+"F57.opExtrude","CAP_FACE",FACE,{"disambiguationData":[OSD([sQuery(id+"F56.wireOp",EDGE,"E50.bottom"),sQuery(id+"F56.wireOp",EDGE,"E50.top"),sQuery(id+"F56.wireOp",EDGE,"E50.left"),sQuery(id+"F56.wireOp",EDGE,"E50.right")])],"isStart":false});
            var sketch = newSketch(context, id + "F62", { "sketchPlane" : qUnion([Q0])});
            skLineSegment(sketch, "E53.bottom", {"start": v(-2176.42, 525) * mm, "end": v(-2776.42, 525) * mm});
            skLineSegment(sketch, "E53.top", {"start": v(-2176.42, 500) * mm, "end": v(-2776.42, 500) * mm});
            skLineSegment(sketch, "E53.left", {"start": v(-2176.42, 525) * mm, "end": v(-2176.42, 500) * mm});
            skLineSegment(sketch, "E53.right", {"start": v(-2776.42, 525) * mm, "end": v(-2776.42, 500) * mm});
            skSolve(sketch);
        }
        {
            var Q0;
            Q0 = qSketchRegion(id + "F62", true);
            var Q1;
            Q1=makeQuery(id+"F55.opExtrude","SWEPT_FACE",FACE,{"disambiguationData":[OSD([sQuery(id+"F54.wireOp",EDGE,"E48.left")])]});
            extrude(context, id + "F63", {"entities" : qUnion([Q0]), "endBound" : BoundingType.UP_TO_SURFACE, "endBoundEntityFace" : qUnion([Q1]), "depth" : 25 * mm});
        }
        {
            var Q0;
            Q0=makeQuery(id+"F59.opExtrude","CAP_FACE",FACE,{"disambiguationData":[OSD([sQuery(id+"F58.wireOp",EDGE,"E51.bottom"),sQuery(id+"F58.wireOp",EDGE,"E51.top"),sQuery(id+"F58.wireOp",EDGE,"E51.left"),sQuery(id+"F58.wireOp",EDGE,"E51.right")])],"isStart":true});
            var sketch = newSketch(context, id + "F64", { "sketchPlane" : qUnion([Q0])});
            skLineSegment(sketch, "E54.bottom", {"start": v(-876.98, 500) * mm, "end": v(163.02, 500) * mm});
            skLineSegment(sketch, "E54.top", {"start": v(-876.98, 450) * mm, "end": v(163.02, 450) * mm});
            skLineSegment(sketch, "E54.left", {"start": v(-876.98, 500) * mm, "end": v(-876.98, 450) * mm});
            skLineSegment(sketch, "E54.right", {"start": v(163.02, 500) * mm, "end": v(163.02, 450) * mm});
            skSolve(sketch);
        }
        {
            var Q0;
            Q0 = qSketchRegion(id + "F64", true);
            extrude(context, id + "F65", {"entities" : qUnion([Q0]), "depth" : 25 * mm});
        }
        {
            var Q0;
            Q0=makeQuery(id+"F63.opExtrude","SWEPT_FACE",FACE,{"disambiguationData":[OSD([sQuery(id+"F62.wireOp",EDGE,"E53.top")])]});
            var sketch = newSketch(context, id + "F66", { "sketchPlane" : qUnion([Q0])});
            skCircle(sketch, "E55", {"center": v(-2236.42, 663.02) * mm, "radius": 30 * mm});
            skSolve(sketch);
        }
        {
            var Q0;
            Q0 = qSketchRegion(id + "F66", true);
            extrude(context, id + "F67", {"entities" : qUnion([Q0]), "endBound" : BoundingType.UP_TO_NEXT, "depth" : 25 * mm});
        }
        {
            var Q0;
            Q0=makeQuery(id+"F53.opExtrude","CAP_EDGE",EDGE,{"disambiguationData":[OSD([sQuery(id+"F52.wireOp",EDGE,"E47.right")])],"isStart":false});
            fillet(context, id + "F68", {"entities" : qUnion([Q0]), "radius" : 50 * mm, "tangentPropagation" : true, "allowEdgeOverflow" : false});
        }
        {
            var Q0;
            Q0=makeQuery(id+"F63.opExtrude","CAP_EDGE",EDGE,{"disambiguationData":[OSD([sQuery(id+"F62.wireOp",EDGE,"E53.left")])],"isStart":false});
            fillet(context, id + "F69", {"entities" : qUnion([Q0]), "radius" : 50 * mm, "tangentPropagation" : true, "allowEdgeOverflow" : false});
        }
        {
            var Q0;
            Q0=makeQuery(id+"F57.opExtrude","CAP_FACE",FACE,{"disambiguationData":[OSD([sQuery(id+"F56.wireOp",EDGE,"E50.bottom"),sQuery(id+"F56.wireOp",EDGE,"E50.top"),sQuery(id+"F56.wireOp",EDGE,"E50.left"),sQuery(id+"F56.wireOp",EDGE,"E50.right")])],"isStart":false});
            var sketch = newSketch(context, id + "F70", { "sketchPlane" : qUnion([Q0])});
            skLineSegment(sketch, "E56.bottom", {"start": v(-2752.54, 1349.23) * mm, "end": v(-1402.08, 1349.23) * mm});
            skLineSegment(sketch, "E56.top", {"start": v(-2752.54, 992.27) * mm, "end": v(-1402.08, 992.27) * mm});
            skLineSegment(sketch, "E56.left", {"start": v(-2752.54, 1349.23) * mm, "end": v(-2752.54, 992.27) * mm});
            skLineSegment(sketch, "E56.right", {"start": v(-1402.08, 1349.23) * mm, "end": v(-1402.08, 992.27) * mm});
            skSolve(sketch);
        }
        {
            var Q0;
            Q0 = qSketchRegion(id + "F70", true);
            extrude(context, id + "F71", {"entities" : qUnion([Q0]), "operationType" : NewBodyOperationType.ADD, "depth" : 300 * mm});
        }
        {
            var Q0;
            Q0=makeQuery(id+"F71.opExtrude","CAP_FACE",FACE,{"disambiguationData":[OSD([sQuery(id+"F70.wireOp",EDGE,"E56.bottom"),sQuery(id+"F70.wireOp",EDGE,"E56.top"),sQuery(id+"F70.wireOp",EDGE,"E56.left"),sQuery(id+"F70.wireOp",EDGE,"E56.right")])],"isStart":false});
            var Q1;
            Q1=makeQuery(id+"F71.opExtrude","SWEPT_FACE",FACE,{"disambiguationData":[OSD([sQuery(id+"F70.wireOp",EDGE,"E56.right")])]});
            var Q2;
            Q2=makeQuery(id+"F71.opExtrude","SWEPT_FACE",FACE,{"disambiguationData":[OSD([sQuery(id+"F70.wireOp",EDGE,"E56.left")])]});
            fillet(context, id + "F72", {"entities" : qUnion([Q0, Q1, Q2]), "radius" : 50 * mm, "tangentPropagation" : true, "allowEdgeOverflow" : false});
        }
    });
